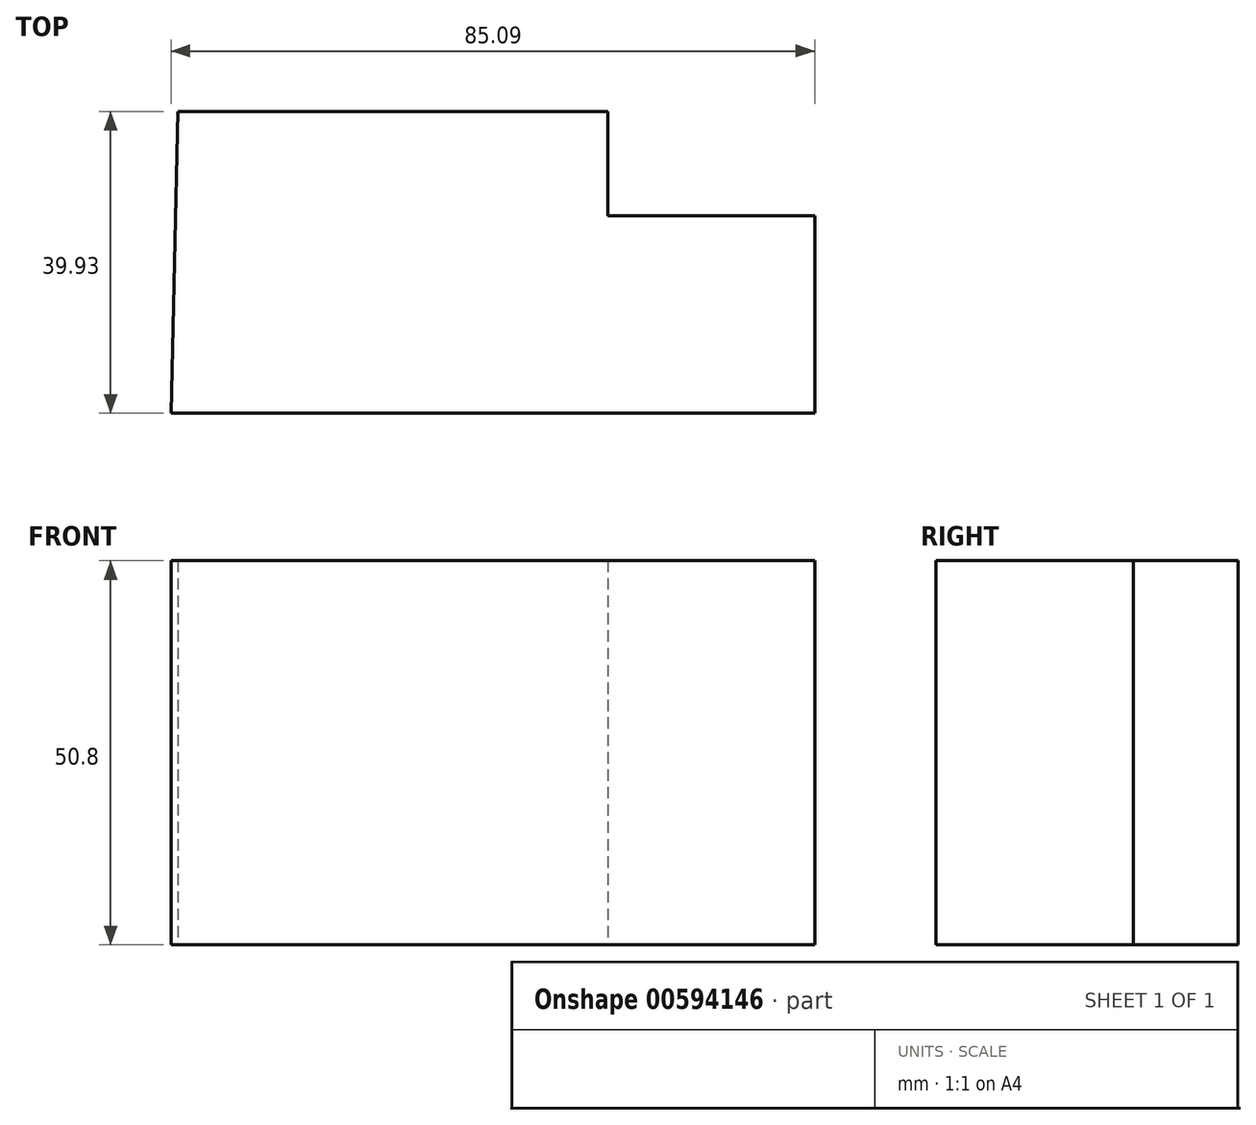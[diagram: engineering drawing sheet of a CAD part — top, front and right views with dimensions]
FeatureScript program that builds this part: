
annotation { "Feature Type Name" : "Feature", "Feature Type Description" : "" }
export const myFeature = defineFeature(function(context is Context, id is Id, definition is map)
    precondition{}
    {
        {
            var Q0;
            Q0=qCreatedBy(makeId("Top.planeOp"),FACE);
            var sketch = newSketch(context, id + "F0", { "sketchPlane" : qUnion([Q0])});
            skLineSegment(sketch, "E0", {"start": v(-23.8, 27.64) * mm, "end": v(33.02, 27.64) * mm});
            skLineSegment(sketch, "E1", {"start": v(33.02, 27.64) * mm, "end": v(33.02, 13.82) * mm});
            skLineSegment(sketch, "E2", {"start": v(33.02, 13.82) * mm, "end": v(60.36, 13.82) * mm});
            skLineSegment(sketch, "E3", {"start": v(60.36, 13.82) * mm, "end": v(60.36, -12.29) * mm});
            skLineSegment(sketch, "E4", {"start": v(60.36, -12.29) * mm, "end": v(-24.73, -12.29) * mm});
            skLineSegment(sketch, "E5", {"start": v(-24.73, -12.29) * mm, "end": v(-23.8, 27.64) * mm});
            skSolve(sketch);
        }
        {
            var Q0;
            Q0=makeQuery(id+"F0.imprint","IMPRINT",FACE,{"disambiguationData":[TD([[makeQuery(id+"F0.imprint","IMPRINT",EDGE,{"derivedFrom":sQuery(id+"F0.wireOp",EDGE,"E0")}),-1.0]])]});
            extrude(context, id + "F1", {"entities" : qUnion([Q0]), "depth" : 50.8 * mm, "offsetDistance" : 25.4 * mm});
        }
    });
